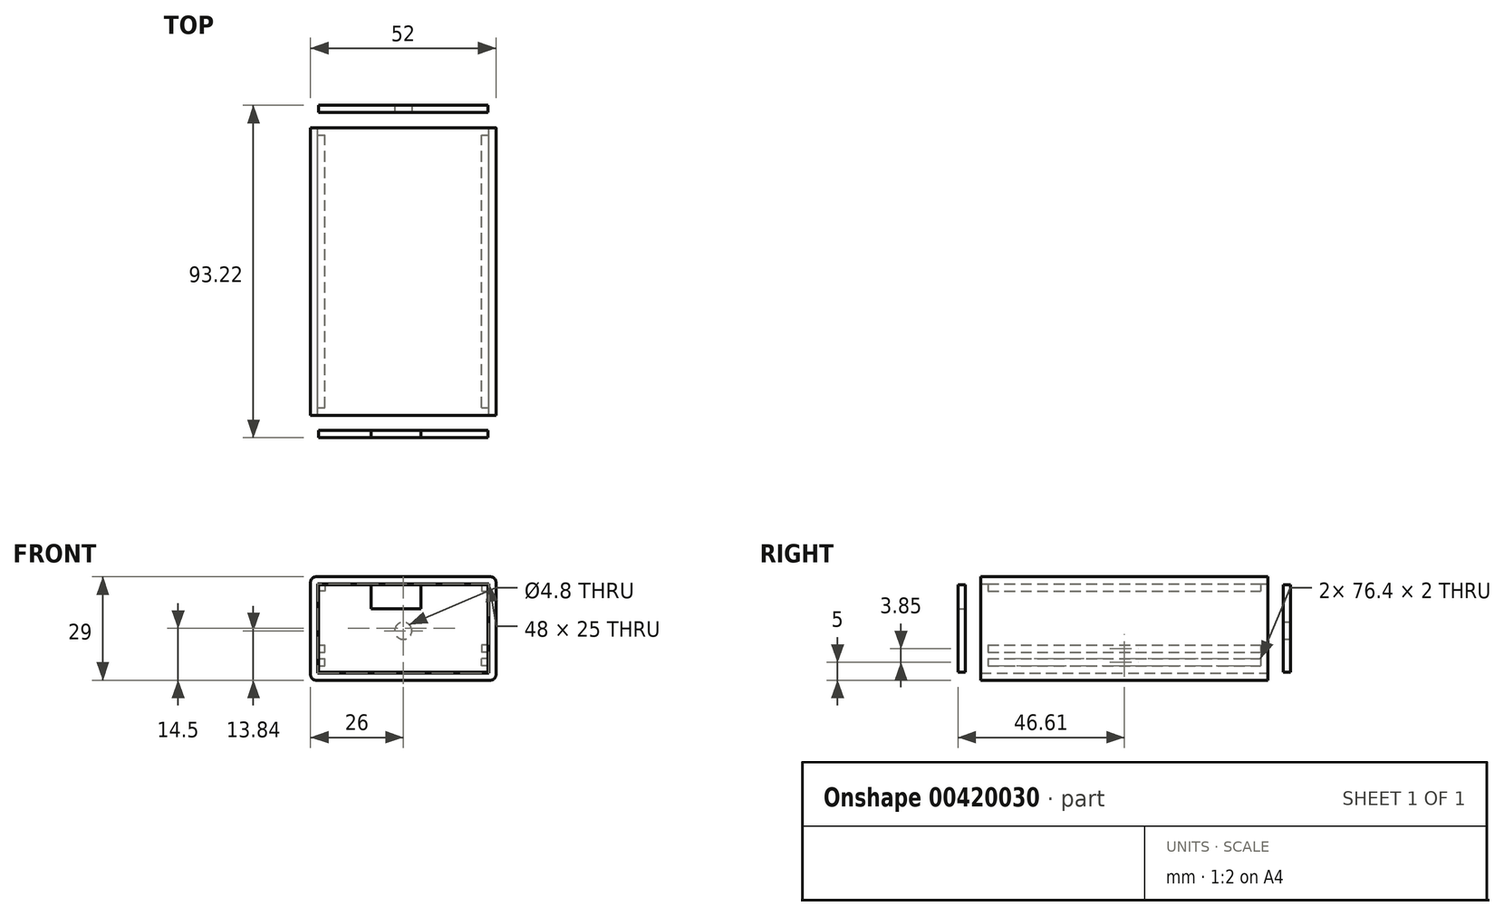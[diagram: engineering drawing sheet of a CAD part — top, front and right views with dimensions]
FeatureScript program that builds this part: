
annotation { "Feature Type Name" : "Feature", "Feature Type Description" : "" }
export const myFeature = defineFeature(function(context is Context, id is Id, definition is map)
    precondition{}
    {
        {
            var Q0;
            Q0=qCreatedBy(makeId("Front.planeOp"),FACE);
            var sketch = newSketch(context, id + "F0", { "sketchPlane" : qUnion([Q0])});
            skLineSegment(sketch, "E0.bottom", {"start": v(-24.5, 29) * mm, "end": v(24.5, 29) * mm});
            skLineSegment(sketch, "E0.top", {"start": v(-24.5, 0) * mm, "end": v(24.5, 0) * mm});
            skLineSegment(sketch, "E0.left", {"start": v(-26, 27.5) * mm, "end": v(-26, 1.5) * mm});
            skLineSegment(sketch, "E0.right", {"start": v(26, 27.5) * mm, "end": v(26, 1.5) * mm});
            skLineSegment(sketch, "E1.bottom", {"start": v(-24, 27) * mm, "end": v(24, 27) * mm});
            skLineSegment(sketch, "E1.top", {"start": v(-24, 2) * mm, "end": v(24, 2) * mm});
            skLineSegment(sketch, "E1.left", {"start": v(-24, 27) * mm, "end": v(-24, 2) * mm});
            skLineSegment(sketch, "E1.right", {"start": v(24, 27) * mm, "end": v(24, 2) * mm});
            skLineSegment(sketch, "E2.bottom", {"start": v(-24, 4) * mm, "end": v(-22, 4) * mm});
            skLineSegment(sketch, "E2.top", {"start": v(-24, 6) * mm, "end": v(-22, 6) * mm});
            skLineSegment(sketch, "E2.left", {"start": v(-24, 4) * mm, "end": v(-24, 6) * mm});
            skLineSegment(sketch, "E2.right", {"start": v(-22, 4) * mm, "end": v(-22, 6) * mm});
            skLineSegment(sketch, "E3.bottom", {"start": v(-24, 7.85) * mm, "end": v(-22, 7.85) * mm});
            skLineSegment(sketch, "E3.top", {"start": v(-24, 9.85) * mm, "end": v(-22, 9.85) * mm});
            skLineSegment(sketch, "E3.left", {"start": v(-24, 7.85) * mm, "end": v(-24, 9.85) * mm});
            skLineSegment(sketch, "E3.right", {"start": v(-22, 7.85) * mm, "end": v(-22, 9.85) * mm});
            skLineSegment(sketch, "E4.bottom", {"start": v(24, 4) * mm, "end": v(22, 4) * mm});
            skLineSegment(sketch, "E4.top", {"start": v(24, 6) * mm, "end": v(22, 6) * mm});
            skLineSegment(sketch, "E4.left", {"start": v(24, 4) * mm, "end": v(24, 6) * mm});
            skLineSegment(sketch, "E4.right", {"start": v(22, 4) * mm, "end": v(22, 6) * mm});
            skLineSegment(sketch, "E5.bottom", {"start": v(24, 9.85) * mm, "end": v(22, 9.85) * mm});
            skLineSegment(sketch, "E5.top", {"start": v(24, 7.85) * mm, "end": v(22, 7.85) * mm});
            skLineSegment(sketch, "E5.left", {"start": v(24, 9.85) * mm, "end": v(24, 7.85) * mm});
            skLineSegment(sketch, "E5.right", {"start": v(22, 9.85) * mm, "end": v(22, 7.85) * mm});
            skLineSegment(sketch, "E6", {"start": v(-22, 27) * mm, "end": v(-22, 25) * mm});
            skLineSegment(sketch, "E7", {"start": v(-22, 25) * mm, "end": v(-24, 25) * mm});
            skLineSegment(sketch, "E8.MirrorCS", {"start": v(22, 27) * mm, "end": v(22, 25) * mm});
            skLineSegment(sketch, "E9.MirrorCS", {"start": v(22, 25) * mm, "end": v(24, 25) * mm});
            skPoint(sketch, "E10.visualSharp", {"position": v(-26, 29) * mm});
            skArc(sketch, "E10.filletArc", {"start": v(-24.5, 29) * mm, "mid": v(-25.56, 28.56) * mm, "end": v(-26, 27.5) * mm});
            skPoint(sketch, "E11.visualSharp", {"position": v(26, 29) * mm});
            skArc(sketch, "E11.filletArc", {"start": v(26, 27.5) * mm, "mid": v(25.56, 28.56) * mm, "end": v(24.5, 29) * mm});
            skPoint(sketch, "E12.visualSharp", {"position": v(26, 0) * mm});
            skArc(sketch, "E12.filletArc", {"start": v(24.5, 0) * mm, "mid": v(25.56, 0.44) * mm, "end": v(26, 1.5) * mm});
            skPoint(sketch, "E13.visualSharp", {"position": v(-26, 0) * mm});
            skArc(sketch, "E13.filletArc", {"start": v(-26, 1.5) * mm, "mid": v(-25.56, 0.44) * mm, "end": v(-24.5, 0) * mm});
            skSolve(sketch);
        }
        {
            var Q0;
            Q0=makeQuery(id+"F0.imprint","IMPRINT",FACE,{"disambiguationData":[TD([[makeQuery(id+"F0.imprint","IMPRINT",EDGE,{"derivedFrom":sQuery(id+"F0.wireOp",EDGE,"E0.bottom")}),-1.0]])]});
            extrude(context, id + "F1", {"entities" : qUnion([Q0]), "endBound" : BoundingType.SYMMETRIC, "depth" : 80.6 * mm});
        }
        {
            var Q0;
            Q0=makeQuery(id+"F0.imprint","IMPRINT",FACE,{"disambiguationData":[TD([[makeQuery(id+"F0.imprint","IMPRINT",EDGE,{"derivedFrom":sQuery(id+"F0.wireOp",EDGE,"E3.bottom")}),1.0]])]});
            var Q1;
            Q1=makeQuery(id+"F0.imprint","IMPRINT",FACE,{"disambiguationData":[TD([[makeQuery(id+"F0.imprint","IMPRINT",EDGE,{"derivedFrom":sQuery(id+"F0.wireOp",EDGE,"E2.bottom")}),1.0]])]});
            var Q2;
            Q2=makeQuery(id+"F0.imprint","IMPRINT",FACE,{"disambiguationData":[TD([[makeQuery(id+"F0.imprint","IMPRINT",EDGE,{"derivedFrom":sQuery(id+"F0.wireOp",EDGE,"E5.bottom")}),1.0]])]});
            var Q3;
            Q3=makeQuery(id+"F0.imprint","IMPRINT",FACE,{"disambiguationData":[TD([[makeQuery(id+"F0.imprint","IMPRINT",EDGE,{"derivedFrom":sQuery(id+"F0.wireOp",EDGE,"E4.bottom")}),-1.0]])]});
            var Q4;
            {var subQ3=sQuery(id+"F0.wireOp",EDGE,"E6");Q4=makeQuery(id+"F0.imprint","IMPRINT",FACE,{"disambiguationData":[TD([[makeQuery(id+"F0.imprint","IMPRINT",EDGE,{"derivedFrom":subQ3}),-1.0]])]});}
            var Q5;
            {var subQ3=sQuery(id+"F0.wireOp",EDGE,"E8.MirrorCS");Q5=makeQuery(id+"F0.imprint","IMPRINT",FACE,{"disambiguationData":[TD([[makeQuery(id+"F0.imprint","IMPRINT",EDGE,{"derivedFrom":subQ3}),1.0]])]});}
            extrude(context, id + "F2", {"entities" : qUnion([Q0, Q1, Q2, Q3, Q4, Q5]), "operationType" : NewBodyOperationType.ADD, "endBound" : BoundingType.SYMMETRIC, "depth" : 76.4 * mm});
        }
        {
            var Q0;
            Q0=qCreatedBy(makeId("Top.planeOp"),FACE);
            var sketch = newSketch(context, id + "F3", { "sketchPlane" : qUnion([Q0])});
            skLineSegment(sketch, "E14.bottom", {"start": v(-23.8, -44.61) * mm, "end": v(0, -44.61) * mm});
            skLineSegment(sketch, "E14.top", {"start": v(-23.8, -46.61) * mm, "end": v(0, -46.61) * mm});
            skLineSegment(sketch, "E14.left", {"start": v(-23.8, -44.61) * mm, "end": v(-23.8, -46.61) * mm});
            skLineSegment(sketch, "E14.right", {"start": v(0, -44.61) * mm, "end": v(0, -46.61) * mm});
            skLineSegment(sketch, "E15.bottom", {"start": v(0, -44.61) * mm, "end": v(23.8, -44.61) * mm});
            skLineSegment(sketch, "E15.top", {"start": v(0, -46.61) * mm, "end": v(23.8, -46.61) * mm});
            skLineSegment(sketch, "E15.right", {"start": v(23.8, -44.61) * mm, "end": v(23.8, -46.61) * mm});
            skLineSegment(sketch, "E16.MirrorCS", {"start": v(-23.8, 44.61) * mm, "end": v(-23.8, 46.61) * mm});
            skLineSegment(sketch, "E17.MirrorCS", {"start": v(-23.8, 44.61) * mm, "end": v(0, 44.61) * mm});
            skLineSegment(sketch, "E18.MirrorCS", {"start": v(-23.8, 46.61) * mm, "end": v(0, 46.61) * mm});
            skLineSegment(sketch, "E19.MirrorCS", {"start": v(0, 44.61) * mm, "end": v(0, 46.61) * mm});
            skLineSegment(sketch, "E20.MirrorCS", {"start": v(0, 44.61) * mm, "end": v(23.8, 44.61) * mm});
            skLineSegment(sketch, "E21.MirrorCS", {"start": v(0, 46.61) * mm, "end": v(23.8, 46.61) * mm});
            skLineSegment(sketch, "E22.MirrorCS", {"start": v(23.8, 44.61) * mm, "end": v(23.8, 46.61) * mm});
            skSolve(sketch);
        }
        {
            var Q0;
            Q0=makeQuery(id+"F3.imprint","IMPRINT",FACE,{"disambiguationData":[TD([[makeQuery(id+"F3.imprint","IMPRINT",EDGE,{"derivedFrom":sQuery(id+"F3.wireOp",EDGE,"E14.bottom")}),-1.0]])]});
            var Q1;
            Q1=makeQuery(id+"F3.imprint","IMPRINT",FACE,{"disambiguationData":[TD([[makeQuery(id+"F3.imprint","IMPRINT",EDGE,{"derivedFrom":sQuery(id+"F3.wireOp",EDGE,"E15.bottom")}),-1.0]])]});
            extrude(context, id + "F4", {"entities" : qUnion([Q0, Q1]), "depth" : 26.8 * mm, "hasSecondDirection" : true, "secondDirectionOppositeDirection" : true, "secondDirectionDepth" : -2.2 * mm});
        }
        {
            var Q0;
            Q0=qCreatedBy(makeId("Front.planeOp"),FACE);
            var sketch = newSketch(context, id + "F5", { "sketchPlane" : qUnion([Q0])});
            skLineSegment(sketch, "E23.bottom", {"start": v(5, 26.9) * mm, "end": v(-9, 26.9) * mm});
            skLineSegment(sketch, "E23.top", {"start": v(5, 20) * mm, "end": v(-9, 20) * mm});
            skLineSegment(sketch, "E23.left", {"start": v(5, 26.9) * mm, "end": v(5, 20) * mm});
            skLineSegment(sketch, "E23.right", {"start": v(-9, 26.9) * mm, "end": v(-9, 20) * mm});
            skPoint(sketch, "E23.middle", {"position": v(0, 23.45) * mm});
            skSolve(sketch);
        }
        {
            var Q0;
            Q0=makeQuery(id+"F5.imprint","IMPRINT",FACE,{"disambiguationData":[TD([[makeQuery(id+"F5.imprint","IMPRINT",EDGE,{"derivedFrom":sQuery(id+"F5.wireOp",EDGE,"E23.bottom")}),1.0]])]});
            extrude(context, id + "F6", {"entities" : qUnion([Q0]), "operationType" : NewBodyOperationType.REMOVE, "oppositeDirection" : true, "depth" : -46.8 * mm});
        }
        {
            var Q0;
            Q0=makeQuery(id+"F3.imprint","IMPRINT",FACE,{"disambiguationData":[TD([[makeQuery(id+"F3.imprint","IMPRINT",EDGE,{"derivedFrom":sQuery(id+"F3.wireOp",EDGE,"E16.MirrorCS")}),-1.0]])]});
            var Q1;
            Q1=makeQuery(id+"F3.imprint","IMPRINT",FACE,{"disambiguationData":[TD([[makeQuery(id+"F3.imprint","IMPRINT",EDGE,{"derivedFrom":sQuery(id+"F3.wireOp",EDGE,"E19.MirrorCS")}),-1.0]])]});
            extrude(context, id + "F7", {"entities" : qUnion([Q0, Q1]), "depth" : 26.8 * mm, "hasSecondDirection" : true, "secondDirectionOppositeDirection" : true, "secondDirectionDepth" : -2.2 * mm});
        }
        {
            var Q0;
            Q0=qCreatedBy(makeId("Front.planeOp"),FACE);
            var sketch = newSketch(context, id + "F8", { "sketchPlane" : qUnion([Q0])});
            skCircle(sketch, "E24", {"center": v(0, 13.84) * mm, "radius": 2.4 * mm});
            skSolve(sketch);
        }
        {
            var Q0;
            Q0=makeQuery(id+"F8.imprint","IMPRINT",FACE,{"disambiguationData":[TD([[makeQuery(id+"F8.imprint","IMPRINT",EDGE,{"derivedFrom":sQuery(id+"F8.wireOp",EDGE,"E24")}),1.0]])]});
            extrude(context, id + "F9", {"entities" : qUnion([Q0]), "operationType" : NewBodyOperationType.REMOVE, "oppositeDirection" : true, "depth" : 48 * mm});
        }
    });
